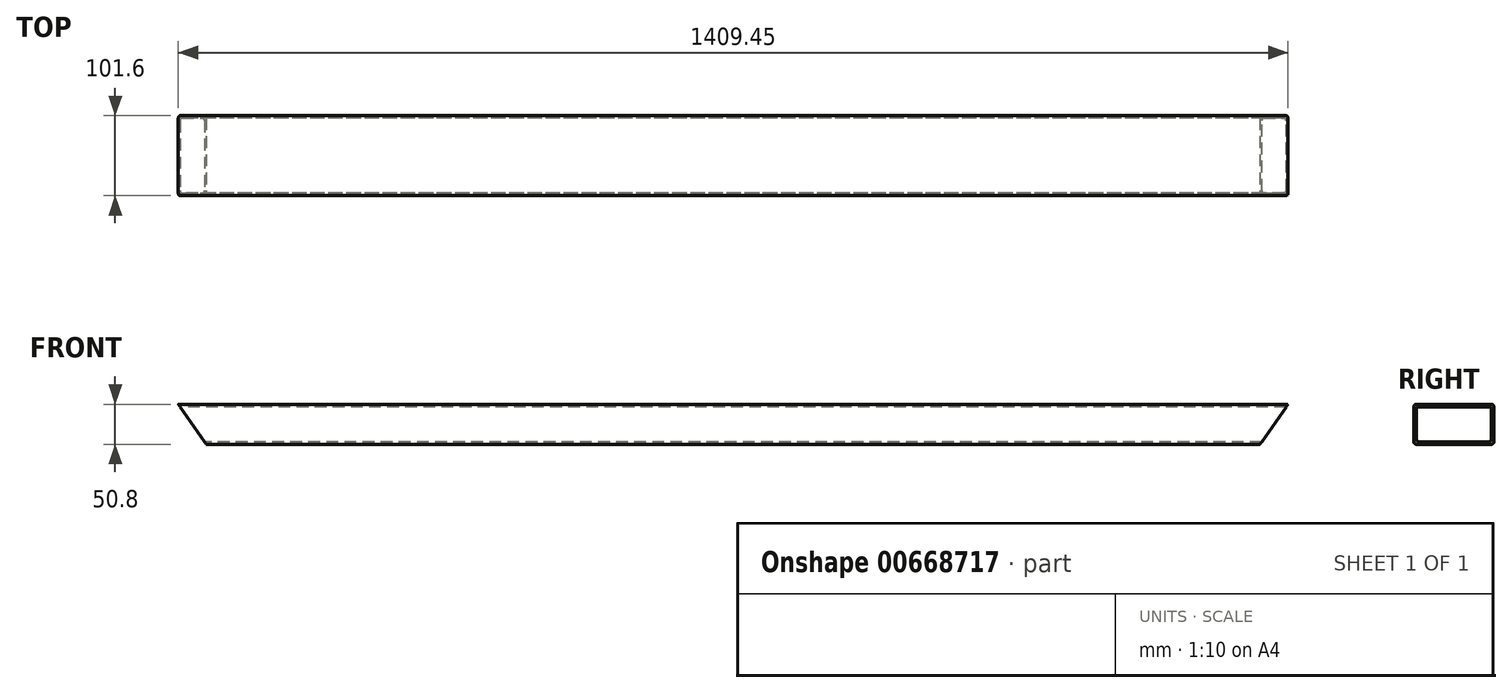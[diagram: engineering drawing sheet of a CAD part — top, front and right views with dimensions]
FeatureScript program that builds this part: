
annotation { "Feature Type Name" : "Feature", "Feature Type Description" : "" }
export const myFeature = defineFeature(function(context is Context, id is Id, definition is map)
    precondition{}
    {
        {
            var Q0;
            Q0=qCreatedBy(makeId("Right.planeOp"),FACE);
            var sketch = newSketch(context, id + "F0", { "sketchPlane" : qUnion([Q0])});
            skLineSegment(sketch, "E0.bottom", {"start": v(47.63, -25.4) * mm, "end": v(-47.62, -25.4) * mm});
            skLineSegment(sketch, "E0.top", {"start": v(47.62, 25.4) * mm, "end": v(-47.63, 25.4) * mm});
            skLineSegment(sketch, "E0.left", {"start": v(50.8, -22.22) * mm, "end": v(50.8, 22.23) * mm});
            skLineSegment(sketch, "E0.right", {"start": v(-50.8, -22.23) * mm, "end": v(-50.8, 22.22) * mm});
            skPoint(sketch, "E0.middle", {"position": v(0, 0) * mm});
            skLineSegment(sketch, "E1.bottom", {"start": v(44.45, 22.23) * mm, "end": v(-44.45, 22.22) * mm});
            skLineSegment(sketch, "E1.top", {"start": v(44.45, -22.22) * mm, "end": v(-44.45, -22.23) * mm});
            skLineSegment(sketch, "E1.left", {"start": v(47.62, 19.05) * mm, "end": v(47.63, -19.05) * mm});
            skLineSegment(sketch, "E1.right", {"start": v(-47.63, 19.05) * mm, "end": v(-47.62, -19.05) * mm});
            skPoint(sketch, "E2.visualSharp", {"position": v(-47.63, 22.22) * mm});
            skArc(sketch, "E2.filletArc", {"start": v(-44.45, 22.22) * mm, "mid": v(-46.7, 21.3) * mm, "end": v(-47.63, 19.05) * mm});
            skPoint(sketch, "E3.visualSharp", {"position": v(-50.8, 25.4) * mm});
            skArc(sketch, "E3.filletArc", {"start": v(-47.63, 25.4) * mm, "mid": v(-49.87, 24.47) * mm, "end": v(-50.8, 22.22) * mm});
            skPoint(sketch, "E4.visualSharp", {"position": v(-47.62, -22.23) * mm});
            skArc(sketch, "E4.filletArc", {"start": v(-47.62, -19.05) * mm, "mid": v(-46.7, -21.3) * mm, "end": v(-44.45, -22.23) * mm});
            skPoint(sketch, "E5.visualSharp", {"position": v(-50.8, -25.4) * mm});
            skArc(sketch, "E5.filletArc", {"start": v(-50.8, -22.23) * mm, "mid": v(-49.87, -24.47) * mm, "end": v(-47.62, -25.4) * mm});
            skPoint(sketch, "E6.visualSharp", {"position": v(47.62, 22.23) * mm});
            skArc(sketch, "E6.filletArc", {"start": v(47.62, 19.05) * mm, "mid": v(46.7, 21.3) * mm, "end": v(44.45, 22.23) * mm});
            skPoint(sketch, "E7.visualSharp", {"position": v(47.63, -22.22) * mm});
            skArc(sketch, "E7.filletArc", {"start": v(44.45, -22.22) * mm, "mid": v(46.7, -21.3) * mm, "end": v(47.63, -19.05) * mm});
            skPoint(sketch, "E8.visualSharp", {"position": v(50.8, -25.4) * mm});
            skArc(sketch, "E8.filletArc", {"start": v(47.63, -25.4) * mm, "mid": v(49.87, -24.47) * mm, "end": v(50.8, -22.22) * mm});
            skPoint(sketch, "E9.visualSharp", {"position": v(50.8, 25.4) * mm});
            skArc(sketch, "E9.filletArc", {"start": v(50.8, 22.23) * mm, "mid": v(49.87, 24.47) * mm, "end": v(47.62, 25.4) * mm});
            skSolve(sketch);
        }
        {
            var Q0;
            Q0=qSketchRegion(id+"F0",true);
            extrude(context, id + "F1", {"entities" : qUnion([Q0]), "depth" : 1409.45 * mm});
        }
        {
            var Q0;
            Q0=qCreatedBy(makeId("Front.planeOp"),FACE);
            var sketch = newSketch(context, id + "F2", { "sketchPlane" : qUnion([Q0])});
            skLineSegment(sketch, "E10", {"start": v(0, -25.4) * mm, "end": v(35.57, -25.4) * mm});
            skLineSegment(sketch, "E11", {"start": v(35.57, -25.4) * mm, "end": v(0, 25.4) * mm});
            skLineSegment(sketch, "E12", {"start": v(0, 25.4) * mm, "end": v(0, -25.4) * mm});
            skLineSegment(sketch, "E13", {"start": v(1373.88, -25.4) * mm, "end": v(1409.45, -25.4) * mm});
            skLineSegment(sketch, "E14", {"start": v(1409.45, -25.4) * mm, "end": v(1409.45, 25.4) * mm});
            skLineSegment(sketch, "E15", {"start": v(1409.45, 25.4) * mm, "end": v(1373.88, -25.4) * mm});
            skSolve(sketch);
        }
        {
            var Q0;
            Q0=qSketchRegion(id+"F2",true);
            extrude(context, id + "F3", {"entities" : qUnion([Q0]), "operationType" : NewBodyOperationType.REMOVE, "endBound" : BoundingType.THROUGH_ALL, "oppositeDirection" : true, "depth" : 25.4 * mm, "hasSecondDirection" : true, "secondDirectionBound" : SecondDirectionBoundingType.THROUGH_ALL, "secondDirectionOppositeDirection" : false, "secondDirectionDepth" : 25.4 * mm});
        }
    });
